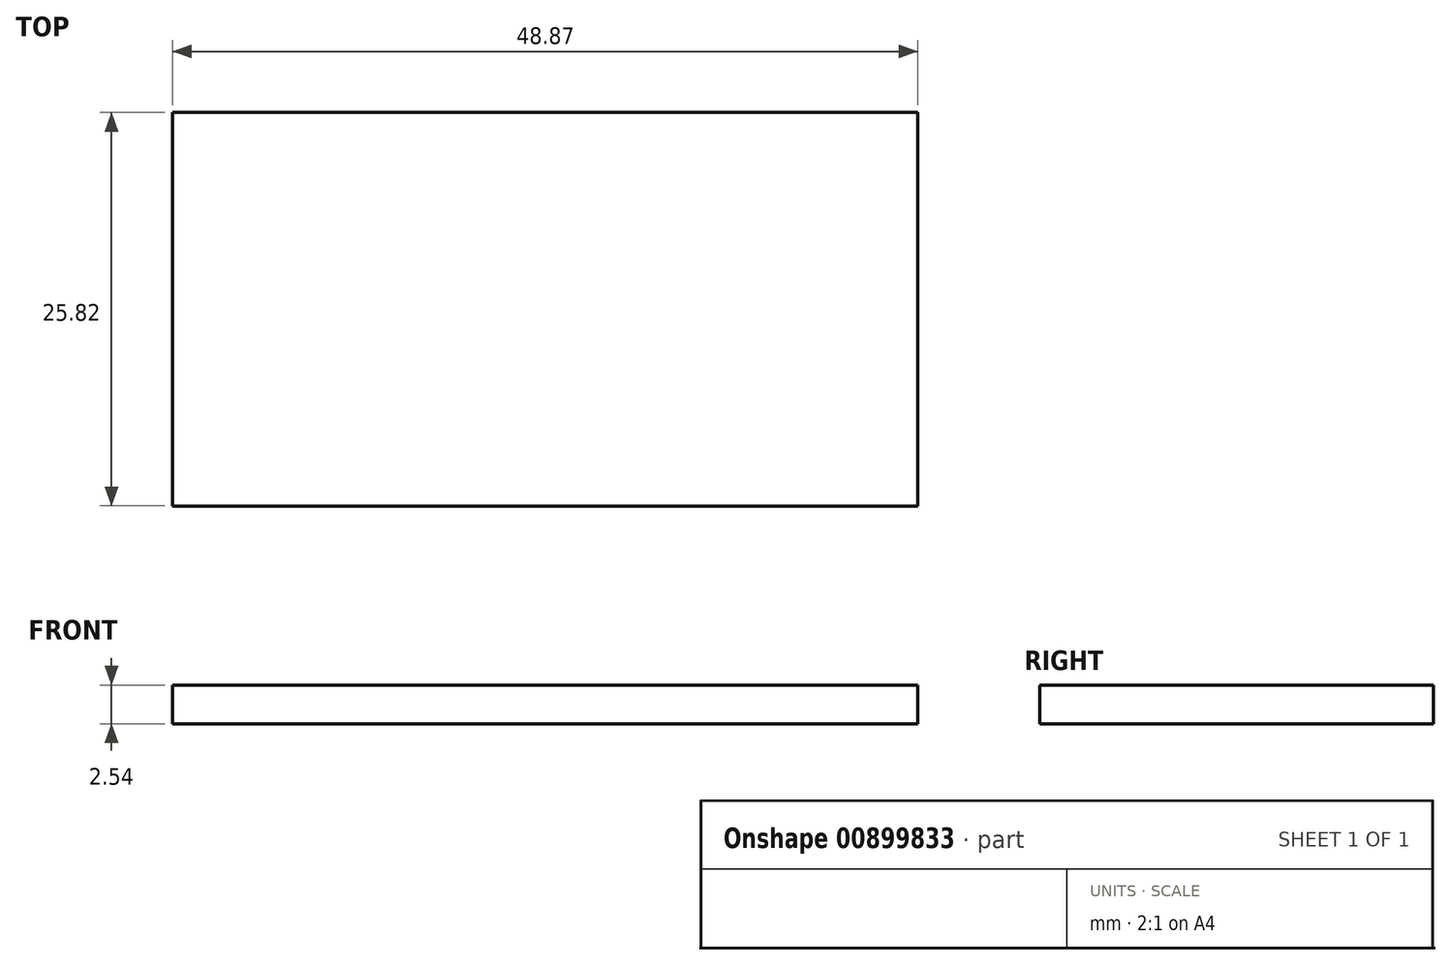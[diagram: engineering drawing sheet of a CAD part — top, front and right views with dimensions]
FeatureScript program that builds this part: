
annotation { "Feature Type Name" : "Feature", "Feature Type Description" : "" }
export const myFeature = defineFeature(function(context is Context, id is Id, definition is map)
    precondition{}
    {
        {
            var Q0;
            Q0=qCreatedBy(makeId("Top.planeOp"),FACE);
            var sketch = newSketch(context, id + "F0", { "sketchPlane" : qUnion([Q0])});
            skLineSegment(sketch, "E0.bottom", {"start": v(-29.56, 19.05) * mm, "end": v(19.3, 19.05) * mm});
            skLineSegment(sketch, "E0.top", {"start": v(-29.56, -6.77) * mm, "end": v(19.3, -6.77) * mm});
            skLineSegment(sketch, "E0.left", {"start": v(-29.56, 19.05) * mm, "end": v(-29.56, -6.77) * mm});
            skLineSegment(sketch, "E0.right", {"start": v(19.3, 19.05) * mm, "end": v(19.3, -6.77) * mm});
            skSolve(sketch);
        }
        {
            var Q0;
            Q0=makeQuery(id+"F0.imprint","IMPRINT",FACE,{"disambiguationData":[TD([[makeQuery(id+"F0.imprint","IMPRINT",EDGE,{"derivedFrom":sQuery(id+"F0.wireOp",EDGE,"E0.bottom")}),-1.0]])]});
            extrude(context, id + "F1", {"entities" : qUnion([Q0]), "depth" : 2.54 * mm, "offsetDistance" : 25.4 * mm});
        }
    });
